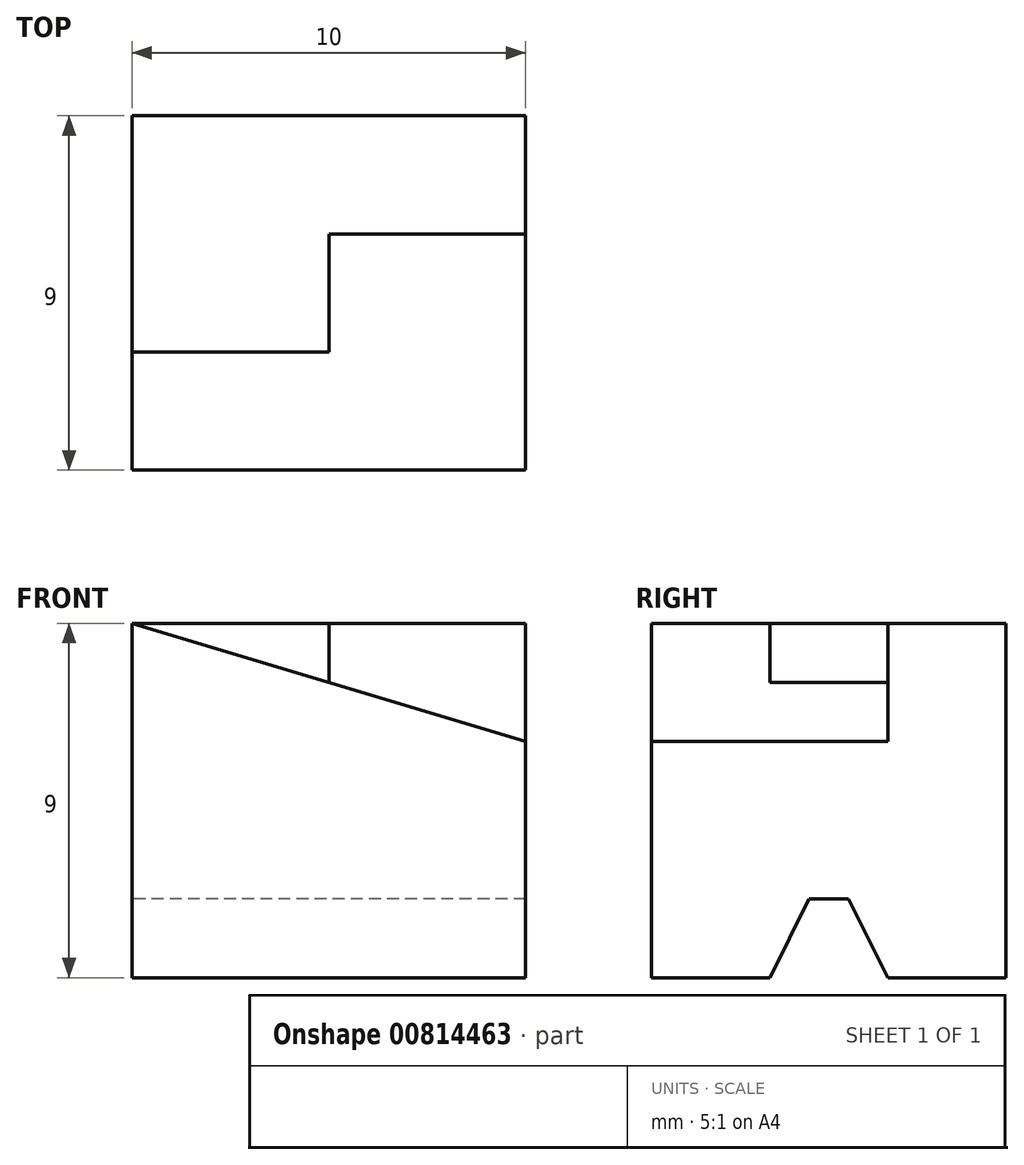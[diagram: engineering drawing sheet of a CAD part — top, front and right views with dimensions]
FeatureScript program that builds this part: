
annotation { "Feature Type Name" : "Feature", "Feature Type Description" : "" }
export const myFeature = defineFeature(function(context is Context, id is Id, definition is map)
    precondition{}
    {
        {
            var Q0;
            Q0=qCreatedBy(makeId("Right.planeOp"),FACE);
            var sketch = newSketch(context, id + "F0", { "sketchPlane" : qUnion([Q0])});
            skLineSegment(sketch, "E0.bottom", {"start": v(0, 0) * mm, "end": v(3, 0) * mm});
            skLineSegment(sketch, "E0.top", {"start": v(0, 9) * mm, "end": v(9, 9) * mm});
            skLineSegment(sketch, "E0.left", {"start": v(0, 0) * mm, "end": v(0, 9) * mm});
            skLineSegment(sketch, "E0.right", {"start": v(9, 0) * mm, "end": v(9, 9) * mm});
            skLineSegment(sketch, "E1", {"start": v(3, 0) * mm, "end": v(4, 2) * mm});
            skLineSegment(sketch, "E2", {"start": v(4.5, 0) * mm, "end": v(4.5, 3.47) * mm, "construction": true});
            skLineSegment(sketch, "E3", {"start": v(4, 2) * mm, "end": v(4.5, 2) * mm});
            skLineSegment(sketch, "E4.MirrorCS", {"start": v(5, 2) * mm, "end": v(4.5, 2) * mm});
            skLineSegment(sketch, "E5.MirrorCS", {"start": v(6, 0) * mm, "end": v(5, 2) * mm});
            skLineSegment(sketch, "E6.trimOffspring", {"start": v(6, 0) * mm, "end": v(9, 0) * mm});
            skSolve(sketch);
        }
        {
            var Q0;
            Q0 = qSketchRegion(id + "F0", true);
            extrude(context, id + "F1", {"entities" : qUnion([Q0]), "depth" : 10 * mm, "offsetDistance" : 25 * mm});
        }
        {
            var Q0;
            Q0=makeQuery(id+"F1.opExtrude","SWEPT_FACE",FACE,{"disambiguationData":[OSD([sQuery(id+"F0.wireOp",EDGE,"E0.left")])]});
            var sketch = newSketch(context, id + "F2", { "sketchPlane" : qUnion([Q0])});
            skLineSegment(sketch, "E7", {"start": v(0, 9) * mm, "end": v(10, 6) * mm});
            skLineSegment(sketch, "E8", {"start": v(5, 9) * mm, "end": v(5, 7.5) * mm});
            skLineSegment(sketch, "E9.0", {"start": v(10, 9) * mm, "end": v(0, 9) * mm});
            skLineSegment(sketch, "E10.0", {"start": v(10, 0) * mm, "end": v(10, 9) * mm});
            skSolve(sketch);
        }
        {
            var Q0;
            Q0 = qSketchRegion(id + "F2", true);
            extrude(context, id + "F3", {"entities" : qUnion([Q0]), "operationType" : NewBodyOperationType.REMOVE, "oppositeDirection" : true, "depth" : 3 * mm, "offsetDistance" : 25 * mm});
        }
        {
            var Q0;
            {var subQ3=sQuery(id+"F2.wireOp",EDGE,"E8");Q0=makeQuery(id+"F2.imprint","IMPRINT",FACE,{"disambiguationData":[TD([[makeQuery(id+"F2.imprint","IMPRINT",EDGE,{"derivedFrom":subQ3}),1.0]])]});}
            extrude(context, id + "F4", {"entities" : qUnion([Q0]), "operationType" : NewBodyOperationType.REMOVE, "oppositeDirection" : true, "depth" : 6 * mm, "offsetDistance" : 25 * mm});
        }
    });
